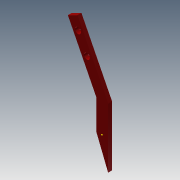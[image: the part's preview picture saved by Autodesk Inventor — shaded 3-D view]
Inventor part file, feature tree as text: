
AUTODESK INVENTOR PART (.ipt)
format: ipt  version: 2013 (Build 170138000, 138)  size: 81,408 bytes
history: native  units: mm
features: sketch x2, extrude x1
ambient origin geometry x8: Origin, YZ Plane, XZ Plane, XY Plane, X Axis, Y Axis, Z Axis, Center Point
bodies: Solid1 (feature_tree)
feature tree (3):
  sketch  "Sketch1"  dims[d12=2.0mm d13=0.0mm]
  sketch  "Sketch2"
  extrude  "Extrusion1"  [1 undecoded]
note: 1 required parameter value undecoded (feature->parameter linkage not recoverable at this tier; creation-order binding heuristic only, values carry confidence <= 0.55)
